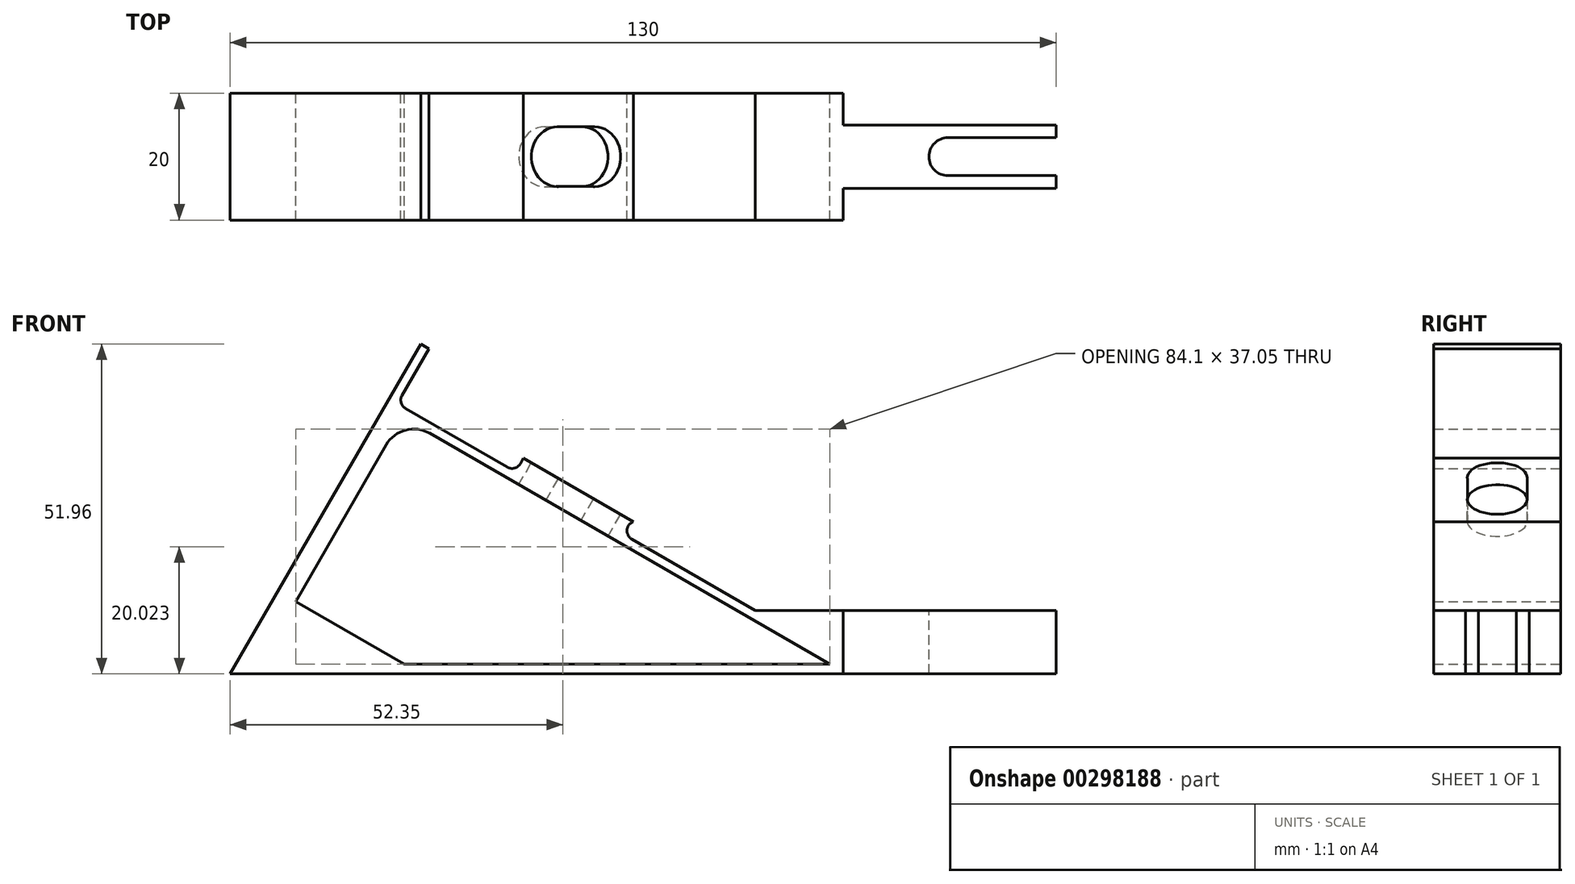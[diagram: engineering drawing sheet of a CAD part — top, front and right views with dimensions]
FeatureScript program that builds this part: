
annotation { "Feature Type Name" : "Feature", "Feature Type Description" : "" }
export const myFeature = defineFeature(function(context is Context, id is Id, definition is map)
    precondition{}
    {
        {
            var Q0;
            Q0=qCreatedBy(makeId("Front.planeOp"),FACE);
            var sketch = newSketch(context, id + "F0", { "sketchPlane" : qUnion([Q0])});
            skLineSegment(sketch, "E0", {"start": v(0, 0) * mm, "end": v(130, 0) * mm});
            skLineSegment(sketch, "E1", {"start": v(130, 0) * mm, "end": v(130, 10) * mm});
            skLineSegment(sketch, "E2", {"start": v(0, 0) * mm, "end": v(30, 51.96) * mm});
            skLineSegment(sketch, "E3", {"start": v(30, 51.96) * mm, "end": v(31.3, 51.21) * mm});
            skLineSegment(sketch, "E4", {"start": v(31.3, 51.21) * mm, "end": v(27.05, 43.85) * mm});
            skLineSegment(sketch, "E5", {"start": v(27.6, 41.8) * mm, "end": v(43.62, 32.55) * mm});
            skLineSegment(sketch, "E6", {"start": v(45.67, 33.1) * mm, "end": v(46.17, 33.97) * mm});
            skLineSegment(sketch, "E7", {"start": v(46.17, 33.97) * mm, "end": v(63.49, 23.97) * mm});
            skLineSegment(sketch, "E8", {"start": v(82.68, 10) * mm, "end": v(130, 10) * mm});
            skArc(sketch, "E9.filletArc", {"start": v(43.62, 32.55) * mm, "mid": v(44.76, 32.4) * mm, "end": v(45.67, 33.1) * mm});
            skArc(sketch, "E10.filletArc", {"start": v(63.49, 23.97) * mm, "mid": v(62.47, 22.7) * mm, "end": v(63.2, 21.24) * mm});
            skLineSegment(sketch, "E11", {"start": v(63.2, 21.24) * mm, "end": v(82.68, 10) * mm});
            skPoint(sketch, "E12.visualSharp", {"position": v(26.3, 42.55) * mm});
            skArc(sketch, "E12.filletArc", {"start": v(27.05, 43.85) * mm, "mid": v(26.9, 42.71) * mm, "end": v(27.6, 41.8) * mm});
            skLineSegment(sketch, "E13", {"start": v(31.38, 37.89) * mm, "end": v(94.4, 1.5) * mm});
            skLineSegment(sketch, "E14", {"start": v(24.55, 36.06) * mm, "end": v(10.3, 11.37) * mm});
            skLineSegment(sketch, "E15", {"start": v(14.55, 8.92) * mm, "end": v(27.4, 1.5) * mm});
            skLineSegment(sketch, "E16", {"start": v(27.4, 1.5) * mm, "end": v(94.4, 1.5) * mm});
            skPoint(sketch, "E17.visualSharp", {"position": v(27.05, 40.39) * mm});
            skArc(sketch, "E17.filletArc", {"start": v(31.38, 37.89) * mm, "mid": v(27.59, 38.39) * mm, "end": v(24.55, 36.06) * mm});
            skLineSegment(sketch, "E18", {"start": v(14.55, 8.92) * mm, "end": v(10.3, 11.37) * mm});
            skSolve(sketch);
        }
        {
            var Q0;
            Q0=makeQuery(id+"F0.imprint","IMPRINT",FACE,{"disambiguationData":[TD([[makeQuery(id+"F0.imprint","IMPRINT",EDGE,{"derivedFrom":sQuery(id+"F0.wireOp",EDGE,"E0")}),1.0]])]});
            extrude(context, id + "F1", {"entities" : qUnion([Q0]), "depth" : 20 * mm});
        }
        {
            var Q0;
            Q0=makeQuery(id+"F1.opExtrude","SWEPT_FACE",FACE,{"disambiguationData":[OSD([sQuery(id+"F0.wireOp",EDGE,"E7")])]});
            var sketch = newSketch(context, id + "F2", { "sketchPlane" : qUnion([Q0])});
            skPoint(sketch, "E19", {"position": v(33, -20) * mm});
            skPoint(sketch, "E20", {"position": v(43, -10) * mm});
            skArc(sketch, "E21", {"start": v(29.15, -5.28) * mm, "mid": v(24.43, -10.1) * mm, "end": v(29.36, -14.71) * mm});
            skArc(sketch, "E22", {"start": v(35.74, -14.71) * mm, "mid": v(40.67, -10.1) * mm, "end": v(35.95, -5.28) * mm});
            skLineSegment(sketch, "E23", {"start": v(29.15, -5.28) * mm, "end": v(35.95, -5.28) * mm});
            skLineSegment(sketch, "E24", {"start": v(29.36, -14.71) * mm, "end": v(35.74, -14.71) * mm});
            skLineSegment(sketch, "E25", {"start": v(29.15, -10) * mm, "end": v(29.15, 0) * mm, "construction": true});
            skLineSegment(sketch, "E26", {"start": v(29.15, 0) * mm, "end": v(29.15, -20) * mm, "construction": true});
            skLineSegment(sketch, "E27", {"start": v(35.95, -10) * mm, "end": v(35.95, 0) * mm, "construction": true});
            skLineSegment(sketch, "E28", {"start": v(35.95, 0) * mm, "end": v(35.95, -20) * mm, "construction": true});
            skSolve(sketch);
        }
        {
            var Q0;
            Q0 = qSketchRegion(id + "F2", true);
            extrude(context, id + "F3", {"entities" : qUnion([Q0]), "operationType" : NewBodyOperationType.REMOVE, "oppositeDirection" : true, "depth" : 4 * mm});
        }
        {
            var Q0;
            Q0=makeQuery(id+"F1.opExtrude","SWEPT_FACE",FACE,{"disambiguationData":[OSD([sQuery(id+"F0.wireOp",EDGE,"E8")])]});
            var sketch = newSketch(context, id + "F4", { "sketchPlane" : qUnion([Q0])});
            skLineSegment(sketch, "E29", {"start": v(96.5, 0) * mm, "end": v(96.5, -5) * mm});
            skLineSegment(sketch, "E30", {"start": v(96.5, -5) * mm, "end": v(130, -5) * mm});
            skLineSegment(sketch, "E31", {"start": v(130, -5) * mm, "end": v(130, -7) * mm});
            skLineSegment(sketch, "E32", {"start": v(130, -7) * mm, "end": v(113, -7) * mm});
            skLineSegment(sketch, "E33", {"start": v(113, -13) * mm, "end": v(130, -13) * mm});
            skLineSegment(sketch, "E34", {"start": v(130, -13) * mm, "end": v(130, -15) * mm});
            skLineSegment(sketch, "E35", {"start": v(130, -15) * mm, "end": v(96.5, -15) * mm});
            skLineSegment(sketch, "E36", {"start": v(96.5, -15) * mm, "end": v(96.5, -20) * mm});
            skArc(sketch, "E37", {"start": v(113, -7) * mm, "mid": v(110, -10) * mm, "end": v(113, -13) * mm});
            skSolve(sketch);
        }
        {
            var Q0;
            {var subQ0=sQuery(id+"F4.wireOp",EDGE,"E29");Q0=makeQuery(id+"F4.imprint","IMPRINT",FACE,{"disambiguationData":[TD([[makeQuery(id+"F4.imprint","IMPRINT",EDGE,{"derivedFrom":subQ0}),1.0]])]});}
            extrude(context, id + "F5", {"entities" : qUnion([Q0]), "operationType" : NewBodyOperationType.REMOVE, "endBound" : BoundingType.THROUGH_ALL, "oppositeDirection" : true, "depth" : 25 * mm});
        }
        {
            var Q0;
            {var subQ0=sQuery(id+"F4.wireOp",EDGE,"E32");Q0=makeQuery(id+"F4.imprint","IMPRINT",FACE,{"disambiguationData":[TD([[makeQuery(id+"F4.imprint","IMPRINT",EDGE,{"derivedFrom":subQ0}),1.0]])]});}
            extrude(context, id + "F6", {"entities" : qUnion([Q0]), "operationType" : NewBodyOperationType.REMOVE, "endBound" : BoundingType.THROUGH_ALL, "oppositeDirection" : true, "depth" : 25 * mm});
        }
        {
            var Q0;
            {var subQ0=sQuery(id+"F4.wireOp",EDGE,"E35");Q0=makeQuery(id+"F4.imprint","IMPRINT",FACE,{"disambiguationData":[TD([[makeQuery(id+"F4.imprint","IMPRINT",EDGE,{"derivedFrom":subQ0}),1.0]])]});}
            extrude(context, id + "F7", {"entities" : qUnion([Q0]), "operationType" : NewBodyOperationType.REMOVE, "endBound" : BoundingType.THROUGH_ALL, "oppositeDirection" : true, "depth" : 25 * mm});
        }
    });
